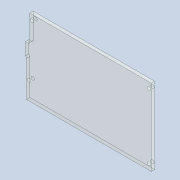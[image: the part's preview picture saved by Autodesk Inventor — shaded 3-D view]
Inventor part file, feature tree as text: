
AUTODESK INVENTOR PART (.ipt)
format: ipt  version: 2020 (Build 240168000, 168)  size: 167,424 bytes
history: native  units: mm
features: reference x6, extrude x3, sketch x3, other x2, fillet x1, hole x1
ambient origin geometry x8: Origin, YZ Plane, XZ Plane, XY Plane, X Axis, Y Axis, Z Axis, Center Point
bodies: Solid1 (feature_tree)
feature tree (16):
  extrude  "Extrusion1"  Depth=108.0mm
  extrude  "Extrusion2"  Depth=3.0mm
  fillet  "Fillet1"  Radius=0.5mm
  extrude  "Extrusion3"  Depth=68.0mm
  hole  "Hole1"  [1 undecoded]
  sketch  "Sketch1"  dims[d0=108.0mm d1=73.0mm]
  sketch  "Sketch2"  dims[d2=3.0mm d3=0.0mm d5=0.5mm d6=0.5mm]
  reference  "Reference1"
  reference  "Reference2"
  reference  "Reference3"
  reference  "Reference4"
  reference  "Reference5"
  reference  "Reference8"
  sketch  "Sketch4"  dims[d7=0.5mm d8=0.5mm d9=3.0mm d10=0.0mm d11=3.0mm d12=6.0mm d13=4.0mm d14=2.0mm d15=90.0deg d16=8.0mm d17=20.594885mm d18=1.5mm d19=2.5mm d22=2.0mm d25=68.0mm d26=0.0mm d27=0.0mm d28=16.0mm d29=5.0mm]
  other  "30-00 Injectomat suplimentar.iam"
  other  "0008-30-002 Corp_Injectomat1:1"
note: 1 required parameter value undecoded (feature->parameter linkage not recoverable at this tier; creation-order binding heuristic only, values carry confidence <= 0.55)
